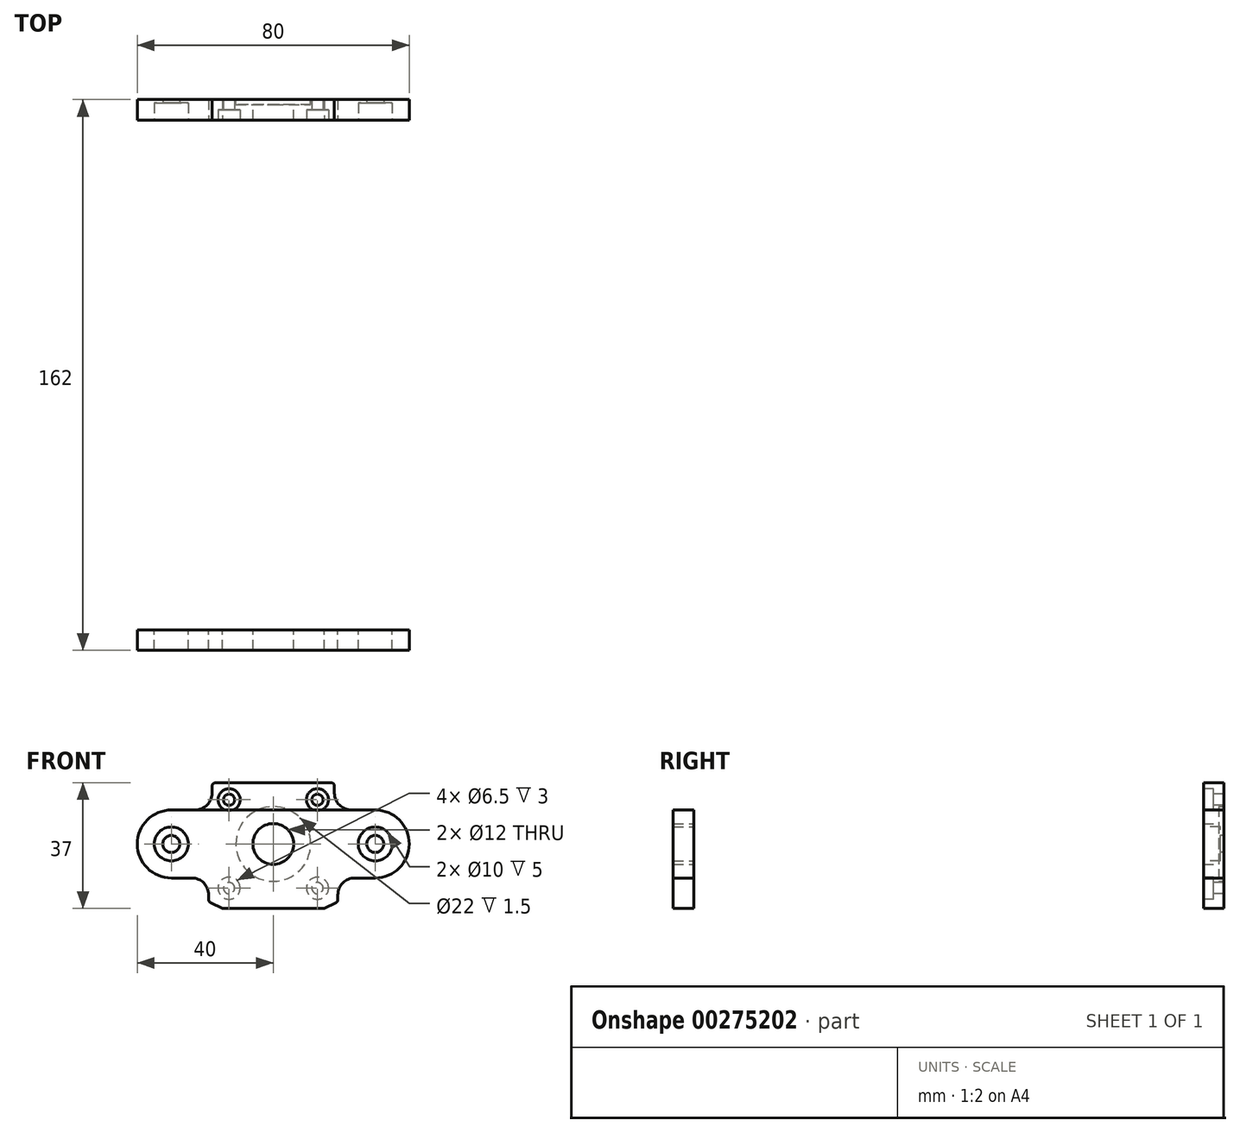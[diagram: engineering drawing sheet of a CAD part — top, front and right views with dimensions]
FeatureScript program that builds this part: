
annotation { "Feature Type Name" : "Feature", "Feature Type Description" : "" }
export const myFeature = defineFeature(function(context is Context, id is Id, definition is map)
    precondition{}
    {
        {
            var Q0;
            Q0=qCreatedBy(makeId("Front.planeOp"),FACE);
            var sketch = newSketch(context, id + "F0", { "sketchPlane" : qUnion([Q0])});
            skCircle(sketch, "E0", {"center": v(-18.7, -0.27) * mm, "radius": 5 * mm});
            skCircle(sketch, "E1", {"center": v(41.3, -0.27) * mm, "radius": 5 * mm});
            skArc(sketch, "E2", {"start": v(-18.7, 9.73) * mm, "mid": v(-28.7, -0.27) * mm, "end": v(-18.7, -10.27) * mm});
            skArc(sketch, "E3", {"start": v(41.3, -10.27) * mm, "mid": v(51.3, -0.27) * mm, "end": v(41.3, 9.73) * mm});
            skLineSegment(sketch, "E4", {"start": v(-18.7, -0.27) * mm, "end": v(41.3, -0.27) * mm, "construction": true});
            skPoint(sketch, "E5", {"position": v(11.3, -0.27) * mm});
            skLineSegment(sketch, "E6", {"start": v(34.3, 9.73) * mm, "end": v(41.3, 9.73) * mm});
            skLineSegment(sketch, "E7", {"start": v(11.3, 16.38) * mm, "end": v(11.3, -27.28) * mm, "construction": true});
            skLineSegment(sketch, "E8", {"start": v(-3.7, -27.27) * mm, "end": v(26.3, -27.27) * mm});
            skLineSegment(sketch, "E9.bottom", {"start": v(24.3, 12.73) * mm, "end": v(-1.7, 12.73) * mm, "construction": true});
            skLineSegment(sketch, "E9.top", {"start": v(24.3, -13.27) * mm, "end": v(-1.7, -13.27) * mm, "construction": true});
            skLineSegment(sketch, "E9.left", {"start": v(24.3, 12.73) * mm, "end": v(24.3, -13.27) * mm, "construction": true});
            skLineSegment(sketch, "E9.right", {"start": v(-1.7, 12.73) * mm, "end": v(-1.7, -13.27) * mm, "construction": true});
            skLineSegment(sketch, "E10.bottom", {"start": v(28.3, 16.73) * mm, "end": v(-5.7, 16.73) * mm, "construction": true});
            skLineSegment(sketch, "E10.top", {"start": v(28.3, -17.27) * mm, "end": v(-5.7, -17.27) * mm, "construction": true});
            skLineSegment(sketch, "E10.left", {"start": v(28.3, 16.73) * mm, "end": v(28.3, -17.27) * mm, "construction": true});
            skLineSegment(sketch, "E10.right", {"start": v(-5.7, 16.73) * mm, "end": v(-5.7, -17.27) * mm, "construction": true});
            skLineSegment(sketch, "E11", {"start": v(-18.7, -10.27) * mm, "end": v(-12.7, -10.27) * mm});
            skLineSegment(sketch, "E12", {"start": v(-3.7, -19.27) * mm, "end": v(-3.7, -27.27) * mm});
            skLineSegment(sketch, "E13", {"start": v(26.3, -27.27) * mm, "end": v(26.3, -19.27) * mm});
            skLineSegment(sketch, "E14", {"start": v(-3.7, -19.27) * mm, "end": v(26.3, -19.27) * mm});
            skLineSegment(sketch, "E15", {"start": v(26.3, -19.27) * mm, "end": v(29.74, -17.55) * mm});
            skLineSegment(sketch, "E16", {"start": v(30.3, -16.65) * mm, "end": v(30.3, -15.27) * mm});
            skLineSegment(sketch, "E17.MirrorCS", {"start": v(-7.7, -16.65) * mm, "end": v(-7.7, -15.27) * mm});
            skLineSegment(sketch, "E18.MirrorCS", {"start": v(-3.7, -19.27) * mm, "end": v(-7.16, -17.55) * mm});
            skLineSegment(sketch, "E19.trimOffspring", {"start": v(35.3, -10.27) * mm, "end": v(41.3, -10.27) * mm});
            skLineSegment(sketch, "E20", {"start": v(-5.7, 17.73) * mm, "end": v(28.3, 17.73) * mm});
            skLineSegment(sketch, "E21", {"start": v(29.3, 16.73) * mm, "end": v(29.3, 14.73) * mm});
            skLineSegment(sketch, "E22", {"start": v(-6.7, 16.73) * mm, "end": v(-6.7, 14.73) * mm});
            skPoint(sketch, "E23.newPointA", {"position": v(29.3, 9.73) * mm});
            skArc(sketch, "E23.filletArc", {"start": v(29.3, 14.73) * mm, "mid": v(30.75, 11.2) * mm, "end": v(34.3, 9.73) * mm});
            skLineSegment(sketch, "E24", {"start": v(-11.7, 9.73) * mm, "end": v(-18.7, 9.73) * mm});
            skPoint(sketch, "E25.visualSharp", {"position": v(-6.7, 9.73) * mm});
            skArc(sketch, "E25.filletArc", {"start": v(-11.7, 9.73) * mm, "mid": v(-8.17, 11.2) * mm, "end": v(-6.7, 14.73) * mm});
            skPoint(sketch, "E26.visualSharp", {"position": v(30.3, -10.27) * mm});
            skArc(sketch, "E26.filletArc", {"start": v(35.3, -10.27) * mm, "mid": v(31.75, -11.73) * mm, "end": v(30.3, -15.27) * mm});
            skPoint(sketch, "E27.visualSharp", {"position": v(-7.7, -10.27) * mm});
            skArc(sketch, "E27.filletArc", {"start": v(-7.7, -15.27) * mm, "mid": v(-9.17, -11.73) * mm, "end": v(-12.7, -10.27) * mm});
            skPoint(sketch, "E28.visualSharp", {"position": v(29.3, 17.73) * mm});
            skArc(sketch, "E28.filletArc", {"start": v(29.3, 16.73) * mm, "mid": v(29, 17.44) * mm, "end": v(28.3, 17.73) * mm});
            skPoint(sketch, "E29.visualSharp", {"position": v(-6.7, 17.73) * mm});
            skArc(sketch, "E29.filletArc", {"start": v(-5.7, 17.73) * mm, "mid": v(-6.42, 17.44) * mm, "end": v(-6.7, 16.73) * mm});
            skPoint(sketch, "E30.visualSharp", {"position": v(30.3, -17.27) * mm});
            skArc(sketch, "E30.filletArc", {"start": v(29.74, -17.55) * mm, "mid": v(30.14, -17.18) * mm, "end": v(30.3, -16.65) * mm});
            skPoint(sketch, "E31.visualSharp", {"position": v(-7.7, -17.27) * mm});
            skArc(sketch, "E31.filletArc", {"start": v(-7.7, -16.65) * mm, "mid": v(-7.56, -17.18) * mm, "end": v(-7.16, -17.55) * mm});
            skPoint(sketch, "E32", {"position": v(-1.7, 12.73) * mm});
            skPoint(sketch, "E33", {"position": v(24.3, 12.73) * mm});
            skPoint(sketch, "E34", {"position": v(-1.7, -13.27) * mm});
            skPoint(sketch, "E35", {"position": v(24.3, -13.27) * mm});
            skSolve(sketch);
        }
        {
            var Q0;
            Q0=makeQuery(id+"F0.imprint","IMPRINT",FACE,{"disambiguationData":[TD([[makeQuery(id+"F0.imprint","IMPRINT",EDGE,{"derivedFrom":sQuery(id+"F0.wireOp",EDGE,"E0")}),-1.0]])]});
            var Q1;
            Q1=makeQuery(id+"F0.imprint","IMPRINT",FACE,{"disambiguationData":[TD([[makeQuery(id+"F0.imprint","IMPRINT",EDGE,{"derivedFrom":sQuery(id+"F0.wireOp",EDGE,"E0")}),1.0]])]});
            var Q2;
            Q2=makeQuery(id+"F0.imprint","IMPRINT",FACE,{"disambiguationData":[TD([[makeQuery(id+"F0.imprint","IMPRINT",EDGE,{"derivedFrom":sQuery(id+"F0.wireOp",EDGE,"E1")}),1.0]])]});
            extrude(context, id + "F1", {"entities" : qUnion([Q0, Q1, Q2]), "oppositeDirection" : true, "depth" : 6 * mm, "offsetDistance" : 25 * mm});
        }
        {
            var Q0;
            Q0=qCreatedBy(makeId("Front.planeOp"),FACE);
            cPlane(context, id + "F2", {"entities" : qUnion([Q0]), "cplaneType" : CPlaneType.OFFSET, "offset" : 150 * mm, "width" : 150 * mm, "height" : 150 * mm});
        }
        {
            var Q0;
            Q0=qCreatedBy(id+"F2.planeOp",FACE);
            var sketch = newSketch(context, id + "F3", { "sketchPlane" : qUnion([Q0])});
            skLineSegment(sketch, "E36.0", {"start": v(-3.7, -19.27) * mm, "end": v(26.3, -19.27) * mm});
            skCircle(sketch, "E36.4", {"center": v(-18.7, -0.27) * mm, "radius": 5 * mm});
            skCircle(sketch, "E36.5", {"center": v(41.3, -0.27) * mm, "radius": 5 * mm});
            skArc(sketch, "E36.6", {"start": v(-18.7, 9.73) * mm, "mid": v(-28.7, -0.27) * mm, "end": v(-18.7, -10.27) * mm});
            skArc(sketch, "E36.7", {"start": v(41.3, -10.27) * mm, "mid": v(51.3, -0.27) * mm, "end": v(41.3, 9.73) * mm});
            skLineSegment(sketch, "E36.9", {"start": v(34.3, 9.73) * mm, "end": v(41.3, 9.73) * mm});
            skLineSegment(sketch, "E36.11", {"start": v(-3.7, -27.27) * mm, "end": v(26.3, -27.27) * mm});
            skLineSegment(sketch, "E36.17", {"start": v(-11.7, 9.73) * mm, "end": v(-18.7, 9.73) * mm});
            skLineSegment(sketch, "E36.18", {"start": v(-18.7, -10.27) * mm, "end": v(-12.7, -10.27) * mm});
            skArc(sketch, "E36.19", {"start": v(-7.7, -15.27) * mm, "mid": v(-9.17, -11.73) * mm, "end": v(-12.7, -10.27) * mm});
            skLineSegment(sketch, "E36.21", {"start": v(35.3, -10.27) * mm, "end": v(41.3, -10.27) * mm});
            skLineSegment(sketch, "E36.23", {"start": v(-3.7, -19.27) * mm, "end": v(-3.7, -27.27) * mm});
            skArc(sketch, "E36.25", {"start": v(35.3, -10.27) * mm, "mid": v(31.75, -11.73) * mm, "end": v(30.3, -15.27) * mm});
            skLineSegment(sketch, "E36.26", {"start": v(26.3, -27.27) * mm, "end": v(26.3, -19.27) * mm});
            skArc(sketch, "E36.27", {"start": v(41.3, -10.27) * mm, "mid": v(51.3, -0.27) * mm, "end": v(41.3, 9.73) * mm});
            skArc(sketch, "E36.28", {"start": v(-7.7, -15.27) * mm, "mid": v(-9.17, -11.73) * mm, "end": v(-12.7, -10.27) * mm});
            skArc(sketch, "E36.29", {"start": v(-18.7, 9.73) * mm, "mid": v(-28.7, -0.27) * mm, "end": v(-18.7, -10.27) * mm});
            skArc(sketch, "E36.30", {"start": v(35.3, -10.27) * mm, "mid": v(31.75, -11.73) * mm, "end": v(30.3, -15.27) * mm});
            skLineSegment(sketch, "E36.31", {"start": v(-3.7, -19.27) * mm, "end": v(-7.16, -17.55) * mm});
            skLineSegment(sketch, "E36.32", {"start": v(26.3, -19.27) * mm, "end": v(29.74, -17.55) * mm});
            skLineSegment(sketch, "E37", {"start": v(-11.7, 9.73) * mm, "end": v(34.3, 9.73) * mm});
            skLineSegment(sketch, "E38", {"start": v(-7.7, -15.27) * mm, "end": v(-7.7, -16.65) * mm});
            skLineSegment(sketch, "E39", {"start": v(30.3, -15.27) * mm, "end": v(30.3, -16.65) * mm});
            skPoint(sketch, "E40.orphan", {"position": v(-7.16, -17.55) * mm});
            skPoint(sketch, "E41.orphan", {"position": v(29.74, -17.55) * mm});
            skArc(sketch, "E42.filletArc", {"start": v(-7.7, -16.65) * mm, "mid": v(-7.56, -17.18) * mm, "end": v(-7.16, -17.55) * mm});
            skArc(sketch, "E43.filletArc", {"start": v(29.74, -17.55) * mm, "mid": v(30.14, -17.18) * mm, "end": v(30.3, -16.65) * mm});
            skPoint(sketch, "E44.0", {"position": v(11.3, -0.27) * mm});
            skSolve(sketch);
        }
        {
            var Q0;
            Q0=sQuery(id+"F0.wireOp",VERTEX,"E32");
            var Q1;
            Q1=sQuery(id+"F0.wireOp",VERTEX,"E33");
            var Q2;
            Q2=sQuery(id+"F0.wireOp",VERTEX,"E34");
            var Q3;
            Q3=sQuery(id+"F0.wireOp",VERTEX,"E35");
            var Q4;
            Q4=makeQuery(id+"F1.opExtrude","SWEPT_BODY",BODY,{"disambiguationData":[OSD([sQuery(id+"F0.wireOp",EDGE,"E0"),sQuery(id+"F0.wireOp",EDGE,"E1"),sQuery(id+"F0.wireOp",EDGE,"E2"),sQuery(id+"F0.wireOp",EDGE,"E3"),sQuery(id+"F0.wireOp",EDGE,"E6"),sQuery(id+"F0.wireOp",EDGE,"E11"),sQuery(id+"F0.wireOp",EDGE,"E14"),sQuery(id+"F0.wireOp",EDGE,"E15"),sQuery(id+"F0.wireOp",EDGE,"E16"),sQuery(id+"F0.wireOp",EDGE,"E17.MirrorCS"),sQuery(id+"F0.wireOp",EDGE,"E18.MirrorCS"),sQuery(id+"F0.wireOp",EDGE,"E19.trimOffspring"),sQuery(id+"F0.wireOp",EDGE,"E20"),sQuery(id+"F0.wireOp",EDGE,"E21"),sQuery(id+"F0.wireOp",EDGE,"E22"),sQuery(id+"F0.wireOp",EDGE,"E23.filletArc"),sQuery(id+"F0.wireOp",EDGE,"E24"),sQuery(id+"F0.wireOp",EDGE,"E25.filletArc"),sQuery(id+"F0.wireOp",EDGE,"E26.filletArc"),sQuery(id+"F0.wireOp",EDGE,"E27.filletArc"),sQuery(id+"F0.wireOp",EDGE,"E28.filletArc"),sQuery(id+"F0.wireOp",EDGE,"E29.filletArc"),sQuery(id+"F0.wireOp",EDGE,"E30.filletArc"),sQuery(id+"F0.wireOp",EDGE,"E31.filletArc")])]});
            hole(context, id + "F4", {"style" : HoleStyle.C_BORE, "endStyle" : HoleEndStyle.BLIND, "standardTappedOrClearance" : lookupTablePath({ "standard" : "ISO", "fit" : "Normal", "size" : "M3", "type" : "Clearance" }), "standardBlindInLast" : lookupTablePath({ "fit" : "Standard", "standard" : "ISO", "size" : "M3", "type" : "Clearance" }), "holeDiameter" : 3.3 * mm, "cBoreDiameter" : 6.5 * mm, "cBoreDepth" : 3 * mm, "holeDepth" : 10.1 * mm, "isTappedThrough" : true, "tappedDepth" : 8 * mm, "tapClearance" : 3, "startFromSketch" : true, "locations" : qUnion([Q0, Q1, Q2, Q3]), "scope" : qUnion([Q4])});
        }
        {
            var Q0;
            Q0=sQuery(id+"F0.wireOp",VERTEX,"E0.center");
            var Q1;
            Q1=sQuery(id+"F0.wireOp",VERTEX,"E1.center");
            var Q2;
            Q2=makeQuery(id+"F1.opExtrude","SWEPT_BODY",BODY,{"disambiguationData":[OSD([sQuery(id+"F0.wireOp",EDGE,"E2"),sQuery(id+"F0.wireOp",EDGE,"E3"),sQuery(id+"F0.wireOp",EDGE,"E6"),sQuery(id+"F0.wireOp",EDGE,"E11"),sQuery(id+"F0.wireOp",EDGE,"E14"),sQuery(id+"F0.wireOp",EDGE,"E15"),sQuery(id+"F0.wireOp",EDGE,"E16"),sQuery(id+"F0.wireOp",EDGE,"E17.MirrorCS"),sQuery(id+"F0.wireOp",EDGE,"E18.MirrorCS"),sQuery(id+"F0.wireOp",EDGE,"E19.trimOffspring"),sQuery(id+"F0.wireOp",EDGE,"E20"),sQuery(id+"F0.wireOp",EDGE,"E21"),sQuery(id+"F0.wireOp",EDGE,"E22"),sQuery(id+"F0.wireOp",EDGE,"E23.filletArc"),sQuery(id+"F0.wireOp",EDGE,"E24"),sQuery(id+"F0.wireOp",EDGE,"E25.filletArc"),sQuery(id+"F0.wireOp",EDGE,"E26.filletArc"),sQuery(id+"F0.wireOp",EDGE,"E27.filletArc"),sQuery(id+"F0.wireOp",EDGE,"E28.filletArc"),sQuery(id+"F0.wireOp",EDGE,"E29.filletArc"),sQuery(id+"F0.wireOp",EDGE,"E30.filletArc"),sQuery(id+"F0.wireOp",EDGE,"E31.filletArc")])]});
            hole(context, id + "F5", {"style" : HoleStyle.C_BORE, "endStyle" : HoleEndStyle.BLIND, "holeDiameter" : 5 * mm, "cBoreDiameter" : 10 * mm, "cBoreDepth" : 5 * mm, "holeDepth" : 10.1 * mm, "isTappedThrough" : true, "tappedDepth" : 8 * mm, "tapClearance" : 3, "startFromSketch" : true, "locations" : qUnion([Q0, Q1]), "scope" : qUnion([Q2])});
        }
        {
            var Q0;
            Q0=makeQuery(id+"F3.imprint","IMPRINT",FACE,{"disambiguationData":[TD([[makeQuery(id+"F3.imprint","IMPRINT",EDGE,{"derivedFrom":sQuery(id+"F3.wireOp",EDGE,"E36.0")}),1.0]])]});
            extrude(context, id + "F6", {"entities" : qUnion([Q0]), "depth" : 6 * mm, "offsetDistance" : 25 * mm});
        }
        {
            var Q0;
            Q0=sQuery(id+"F3.wireOp",VERTEX,"E44.0");
            var Q1;
            Q1=makeQuery(id+"F6.opExtrude","SWEPT_BODY",BODY,{"disambiguationData":[OSD([sQuery(id+"F3.wireOp",EDGE,"E36.0"),sQuery(id+"F3.wireOp",EDGE,"E36.4"),sQuery(id+"F3.wireOp",EDGE,"E36.5"),sQuery(id+"F3.wireOp",EDGE,"E36.9"),sQuery(id+"F3.wireOp",EDGE,"E36.17"),sQuery(id+"F3.wireOp",EDGE,"E36.18"),sQuery(id+"F3.wireOp",EDGE,"E36.21"),sQuery(id+"F3.wireOp",EDGE,"E36.27"),sQuery(id+"F3.wireOp",EDGE,"E36.28"),sQuery(id+"F3.wireOp",EDGE,"E36.29"),sQuery(id+"F3.wireOp",EDGE,"E36.30"),sQuery(id+"F3.wireOp",EDGE,"E36.31"),sQuery(id+"F3.wireOp",EDGE,"E36.32"),sQuery(id+"F3.wireOp",EDGE,"E37"),sQuery(id+"F3.wireOp",EDGE,"E38"),sQuery(id+"F3.wireOp",EDGE,"E39"),sQuery(id+"F3.wireOp",EDGE,"E42.filletArc"),sQuery(id+"F3.wireOp",EDGE,"E43.filletArc")])]});
            hole(context, id + "F7", {"style" : HoleStyle.SIMPLE, "endStyle" : HoleEndStyle.BLIND, "oppositeDirection" : true, "holeDiameter" : 12 * mm, "holeDepth" : 10.1 * mm, "isTappedThrough" : true, "tappedDepth" : 8 * mm, "tapClearance" : 3, "startFromSketch" : true, "locations" : qUnion([Q0]), "scope" : qUnion([Q1])});
        }
        {
            var Q0;
            Q0=makeQuery(id+"F1.opExtrude","CAP_FACE",FACE,{"disambiguationData":[OSD([sQuery(id+"F0.wireOp",EDGE,"E2"),sQuery(id+"F0.wireOp",EDGE,"E3"),sQuery(id+"F0.wireOp",EDGE,"E6"),sQuery(id+"F0.wireOp",EDGE,"E11"),sQuery(id+"F0.wireOp",EDGE,"E14"),sQuery(id+"F0.wireOp",EDGE,"E15"),sQuery(id+"F0.wireOp",EDGE,"E16"),sQuery(id+"F0.wireOp",EDGE,"E17.MirrorCS"),sQuery(id+"F0.wireOp",EDGE,"E18.MirrorCS"),sQuery(id+"F0.wireOp",EDGE,"E19.trimOffspring"),sQuery(id+"F0.wireOp",EDGE,"E20"),sQuery(id+"F0.wireOp",EDGE,"E21"),sQuery(id+"F0.wireOp",EDGE,"E22"),sQuery(id+"F0.wireOp",EDGE,"E23.filletArc"),sQuery(id+"F0.wireOp",EDGE,"E24"),sQuery(id+"F0.wireOp",EDGE,"E25.filletArc"),sQuery(id+"F0.wireOp",EDGE,"E26.filletArc"),sQuery(id+"F0.wireOp",EDGE,"E27.filletArc"),sQuery(id+"F0.wireOp",EDGE,"E28.filletArc"),sQuery(id+"F0.wireOp",EDGE,"E29.filletArc"),sQuery(id+"F0.wireOp",EDGE,"E30.filletArc"),sQuery(id+"F0.wireOp",EDGE,"E31.filletArc")])],"isStart":false});
            var sketch = newSketch(context, id + "F8", { "sketchPlane" : qUnion([Q0])});
            skPoint(sketch, "E45.0", {"position": v(-11.3, -0.27) * mm});
            skSolve(sketch);
        }
        {
            var Q0;
            Q0=sQuery(id+"F8.wireOp",VERTEX,"E45.0");
            var Q1;
            Q1=makeQuery(id+"F1.opExtrude","SWEPT_BODY",BODY,{"disambiguationData":[OSD([sQuery(id+"F0.wireOp",EDGE,"E2"),sQuery(id+"F0.wireOp",EDGE,"E3"),sQuery(id+"F0.wireOp",EDGE,"E6"),sQuery(id+"F0.wireOp",EDGE,"E11"),sQuery(id+"F0.wireOp",EDGE,"E14"),sQuery(id+"F0.wireOp",EDGE,"E15"),sQuery(id+"F0.wireOp",EDGE,"E16"),sQuery(id+"F0.wireOp",EDGE,"E17.MirrorCS"),sQuery(id+"F0.wireOp",EDGE,"E18.MirrorCS"),sQuery(id+"F0.wireOp",EDGE,"E19.trimOffspring"),sQuery(id+"F0.wireOp",EDGE,"E20"),sQuery(id+"F0.wireOp",EDGE,"E21"),sQuery(id+"F0.wireOp",EDGE,"E22"),sQuery(id+"F0.wireOp",EDGE,"E23.filletArc"),sQuery(id+"F0.wireOp",EDGE,"E24"),sQuery(id+"F0.wireOp",EDGE,"E25.filletArc"),sQuery(id+"F0.wireOp",EDGE,"E26.filletArc"),sQuery(id+"F0.wireOp",EDGE,"E27.filletArc"),sQuery(id+"F0.wireOp",EDGE,"E28.filletArc"),sQuery(id+"F0.wireOp",EDGE,"E29.filletArc"),sQuery(id+"F0.wireOp",EDGE,"E30.filletArc"),sQuery(id+"F0.wireOp",EDGE,"E31.filletArc")])]});
            hole(context, id + "F9", {"style" : HoleStyle.C_BORE, "endStyle" : HoleEndStyle.BLIND, "holeDiameter" : 12 * mm, "cBoreDiameter" : 22 * mm, "cBoreDepth" : 1.5 * mm, "holeDepth" : 10.1 * mm, "isTappedThrough" : true, "tappedDepth" : 8 * mm, "tapClearance" : 3, "startFromSketch" : true, "locations" : qUnion([Q0]), "scope" : qUnion([Q1])});
        }
    });
